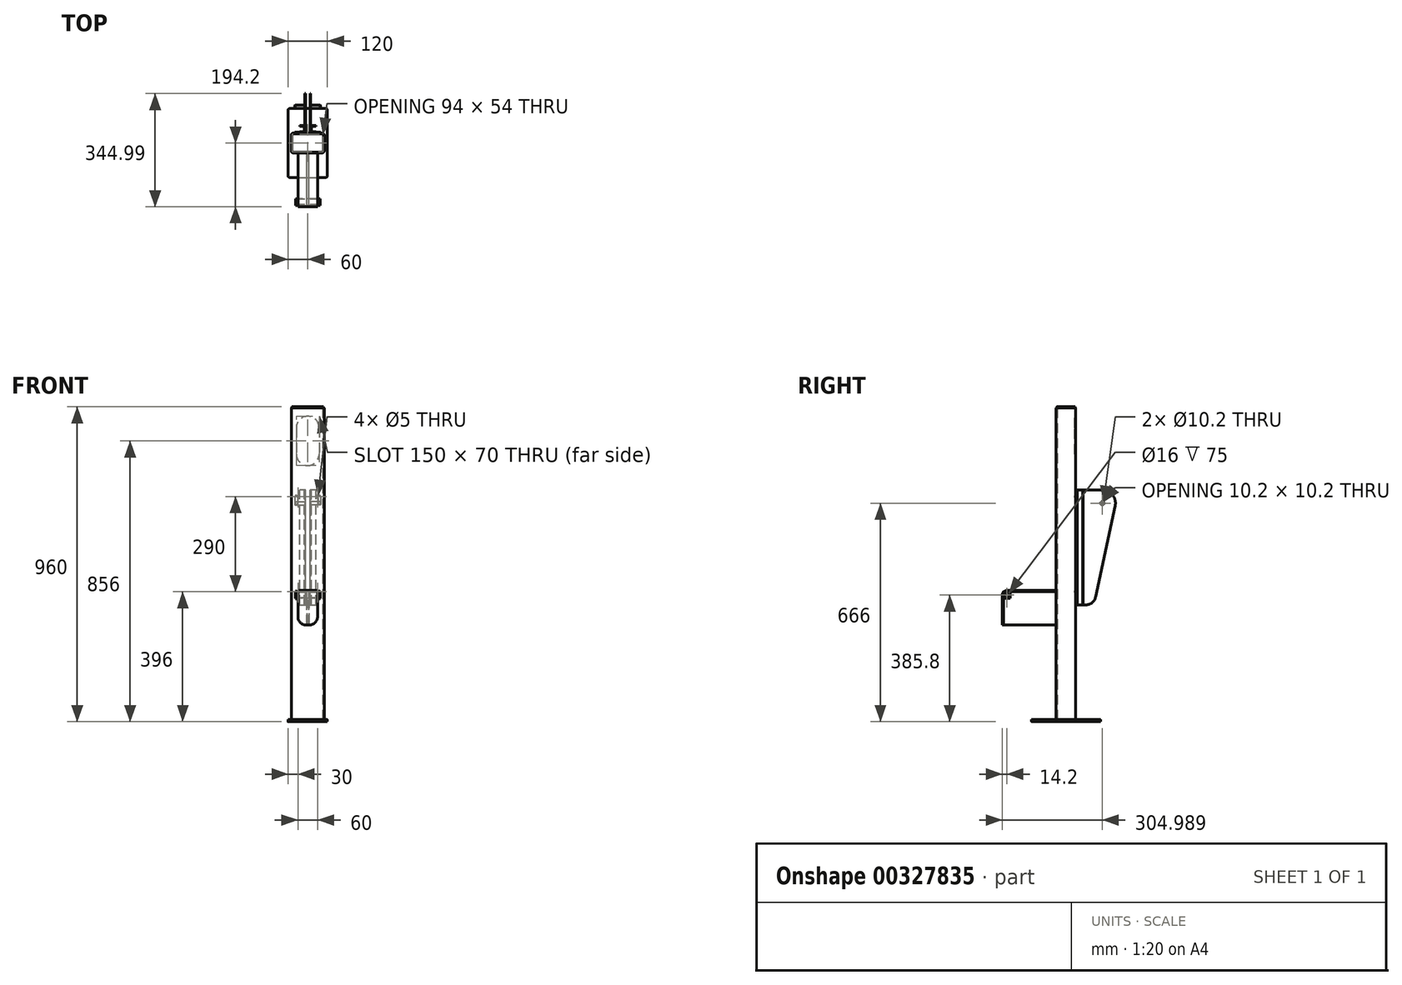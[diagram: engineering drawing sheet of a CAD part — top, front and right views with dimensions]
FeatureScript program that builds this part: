
annotation { "Feature Type Name" : "Feature", "Feature Type Description" : "" }
export const myFeature = defineFeature(function(context is Context, id is Id, definition is map)
    precondition{}
    {
        {
            var Q0;
            Q0=qCreatedBy(makeId("Top.planeOp"),FACE);
            var sketch = newSketch(context, id + "F0", { "sketchPlane" : qUnion([Q0])});
            skLineSegment(sketch, "E0.bottom", {"start": v(50, -30) * mm, "end": v(-50, -30) * mm});
            skLineSegment(sketch, "E0.top", {"start": v(50, 30) * mm, "end": v(-50, 30) * mm});
            skLineSegment(sketch, "E0.left", {"start": v(50, -30) * mm, "end": v(50, 30) * mm});
            skLineSegment(sketch, "E0.right", {"start": v(-50, -30) * mm, "end": v(-50, 30) * mm});
            skPoint(sketch, "E0.middle", {"position": v(0, 0) * mm});
            skSolve(sketch);
        }
        {
            var Q0;
            Q0=makeQuery(id+"F0.imprint","IMPRINT",FACE,{"disambiguationData":[TD([[makeQuery(id+"F0.imprint","IMPRINT",EDGE,{"derivedFrom":sQuery(id+"F0.wireOp",EDGE,"E0.bottom")}),-1.0]])]});
            extrude(context, id + "F1", {"entities" : qUnion([Q0]), "depth" : 950 * mm});
        }
        {
            var Q0;
            Q0=makeQuery(id+"F1.opExtrude","SWEPT_EDGE",EDGE,{"disambiguationData":[OSD([sQuery(id+"F0.wireOp",EDGE,"E0.bottom"),sQuery(id+"F0.wireOp",EDGE,"E0.right")])]});
            var Q1;
            Q1=makeQuery(id+"F1.opExtrude","SWEPT_EDGE",EDGE,{"disambiguationData":[OSD([sQuery(id+"F0.wireOp",EDGE,"E0.top"),sQuery(id+"F0.wireOp",EDGE,"E0.right")])]});
            var Q2;
            Q2=makeQuery(id+"F1.opExtrude","SWEPT_EDGE",EDGE,{"disambiguationData":[OSD([sQuery(id+"F0.wireOp",EDGE,"E0.bottom"),sQuery(id+"F0.wireOp",EDGE,"E0.left")])]});
            var Q3;
            Q3=makeQuery(id+"F1.opExtrude","SWEPT_EDGE",EDGE,{"disambiguationData":[OSD([sQuery(id+"F0.wireOp",EDGE,"E0.top"),sQuery(id+"F0.wireOp",EDGE,"E0.left")])]});
            fillet(context, id + "F2", {"entities" : qUnion([Q0, Q1, Q2, Q3]), "radius" : 5 * mm, "tangentPropagation" : true, "allowEdgeOverflow" : false});
        }
        {
            var Q0;
            Q0=makeQuery(id+"F1.opExtrude","CAP_FACE",FACE,{"disambiguationData":[OSD([sQuery(id+"F0.wireOp",EDGE,"E0.bottom"),sQuery(id+"F0.wireOp",EDGE,"E0.top"),sQuery(id+"F0.wireOp",EDGE,"E0.left"),sQuery(id+"F0.wireOp",EDGE,"E0.right")])],"isStart":true});
            var Q1;
            Q1=makeQuery(id+"F1.opExtrude","CAP_FACE",FACE,{"disambiguationData":[OSD([sQuery(id+"F0.wireOp",EDGE,"E0.bottom"),sQuery(id+"F0.wireOp",EDGE,"E0.top"),sQuery(id+"F0.wireOp",EDGE,"E0.left"),sQuery(id+"F0.wireOp",EDGE,"E0.right")])],"isStart":false});
            shell(context, id + "F3", {"entities" : qUnion([Q0, Q1]), "thickness" : 3 * mm});
        }
        {
            var Q0;
            Q0=makeQuery(id+"F1.opExtrude","SWEPT_FACE",FACE,{"disambiguationData":[OSD([sQuery(id+"F0.wireOp",EDGE,"E0.top")])]});
            var sketch = newSketch(context, id + "F4", { "sketchPlane" : qUnion([Q0])});
            skLineSegment(sketch, "E1", {"start": v(0, 890) * mm, "end": v(0, 810) * mm, "construction": true});
            skArc(sketch, "E2.0.startCap", {"start": v(-35, 890) * mm, "mid": v(0, 925) * mm, "end": v(35, 890) * mm});
            skArc(sketch, "E2.0.endCap", {"start": v(35, 810) * mm, "mid": v(0, 775) * mm, "end": v(-35, 810) * mm});
            skLineSegment(sketch, "E2.0.left", {"start": v(35, 890) * mm, "end": v(35, 810) * mm});
            skLineSegment(sketch, "E2.0.right", {"start": v(-35, 890) * mm, "end": v(-35, 810) * mm});
            skSolve(sketch);
        }
        {
            var Q0;
            Q0 = qSketchRegion(id + "F4", true);
            extrude(context, id + "F5", {"entities" : qUnion([Q0]), "operationType" : NewBodyOperationType.REMOVE, "oppositeDirection" : true, "depth" : 25 * mm});
        }
        {
            var Q0;
            Q0=makeQuery(id+"F1.opExtrude","CAP_FACE",FACE,{"disambiguationData":[OSD([sQuery(id+"F0.wireOp",EDGE,"E0.bottom"),sQuery(id+"F0.wireOp",EDGE,"E0.top"),sQuery(id+"F0.wireOp",EDGE,"E0.left"),sQuery(id+"F0.wireOp",EDGE,"E0.right")])],"isStart":false});
            var sketch = newSketch(context, id + "F6", { "sketchPlane" : qUnion([Q0])});
            skLineSegment(sketch, "E3.bottom", {"start": v(-45, 28) * mm, "end": v(45, 28) * mm});
            skLineSegment(sketch, "E3.top", {"start": v(-45, -28) * mm, "end": v(45, -28) * mm});
            skLineSegment(sketch, "E3.left", {"start": v(-48, 25) * mm, "end": v(-48, -25) * mm});
            skLineSegment(sketch, "E3.right", {"start": v(48, 25) * mm, "end": v(48, -25) * mm});
            skPoint(sketch, "E3.middle", {"position": v(0, 0) * mm});
            skPoint(sketch, "E4.visualSharp", {"position": v(-48, -28) * mm});
            skArc(sketch, "E4.filletArc", {"start": v(-48, -25) * mm, "mid": v(-47.12, -27.12) * mm, "end": v(-45, -28) * mm});
            skPoint(sketch, "E5.visualSharp", {"position": v(48, 28) * mm});
            skArc(sketch, "E5.filletArc", {"start": v(48, 25) * mm, "mid": v(47.12, 27.12) * mm, "end": v(45, 28) * mm});
            skPoint(sketch, "E6.visualSharp", {"position": v(-48, 28) * mm});
            skArc(sketch, "E6.filletArc", {"start": v(-45, 28) * mm, "mid": v(-47.12, 27.12) * mm, "end": v(-48, 25) * mm});
            skPoint(sketch, "E7.visualSharp", {"position": v(48, -28) * mm});
            skArc(sketch, "E7.filletArc", {"start": v(45, -28) * mm, "mid": v(47.12, -27.12) * mm, "end": v(48, -25) * mm});
            skSolve(sketch);
        }
        {
            var Q0;
            Q0=makeQuery(id+"F6.imprint","IMPRINT",FACE,{"disambiguationData":[TD([[makeQuery(id+"F6.imprint","IMPRINT",EDGE,{"derivedFrom":sQuery(id+"F6.wireOp",EDGE,"E3.bottom")}),-1.0]])]});
            var Q1;
            {var subQ3=sQuery(id+"F0.wireOp",EDGE,"E0.bottom");Q1=makeQuery(id+"F6.imprint","IMPRINT",FACE,{"disambiguationData":[TD([[makeQuery(id+"F6.imprint","IMPRINT",EDGE,{"derivedFrom":makeQuery(id+"F3.opShell","OFFSET_EDGE",EDGE,{"disambiguationData":[OSD([subQ3]),TDD([makeQuery(id+"F1.opExtrude","CAP_EDGE",EDGE,{"disambiguationData":[OSD([subQ3])],"isStart":false})])]})}),-1.0]])]});}
            extrude(context, id + "F7", {"entities" : qUnion([Q0, Q1]), "depth" : 4 * mm});
        }
        {
            var Q0;
            Q0=makeQuery(id+"F7.opExtrude","CAP_FACE",FACE,{"disambiguationData":[OSD([sQuery(id+"F6.wireOp",EDGE,"E3.bottom"),sQuery(id+"F6.wireOp",EDGE,"E3.top"),sQuery(id+"F6.wireOp",EDGE,"E3.left"),sQuery(id+"F6.wireOp",EDGE,"E3.right"),sQuery(id+"F6.wireOp",EDGE,"E4.filletArc"),sQuery(id+"F6.wireOp",EDGE,"E5.filletArc"),sQuery(id+"F6.wireOp",EDGE,"E6.filletArc"),sQuery(id+"F6.wireOp",EDGE,"E7.filletArc")])],"isStart":false});
            cPlane(context, id + "F8", {"entities" : qUnion([Q0]), "cplaneType" : CPlaneType.OFFSET, "offset" : 254 * mm, "oppositeDirection" : true, "width" : 150 * mm, "height" : 150 * mm});
        }
        {
            var Q0;
            Q0=qCreatedBy(id+"F8.planeOp",FACE);
            var sketch = newSketch(context, id + "F9", { "sketchPlane" : qUnion([Q0])});
            skLineSegment(sketch, "E8", {"start": v(-45, 32.79) * mm, "end": v(-10.5, 32.79) * mm});
            skLineSegment(sketch, "E9", {"start": v(-9, 34.3) * mm, "end": v(-9, 190.79) * mm});
            skLineSegment(sketch, "E10.0", {"start": v(-7, 34.3) * mm, "end": v(-7, 190.79) * mm});
            skLineSegment(sketch, "E10.1", {"start": v(-45, 30.79) * mm, "end": v(-10.5, 30.79) * mm});
            skPoint(sketch, "E11.visualSharp", {"position": v(-9, 32.79) * mm});
            skArc(sketch, "E11.filletArc", {"start": v(-10.5, 32.79) * mm, "mid": v(-9.44, 33.23) * mm, "end": v(-9, 34.3) * mm});
            skLineSegment(sketch, "E12", {"start": v(-7, 190.79) * mm, "end": v(-9, 190.79) * mm});
            skLineSegment(sketch, "E13", {"start": v(-45, 30.79) * mm, "end": v(-45, 32.79) * mm});
            skArc(sketch, "E14.0", {"start": v(-10.5, 30.79) * mm, "mid": v(-8.03, 31.82) * mm, "end": v(-7, 34.3) * mm});
            skSolve(sketch);
        }
        {
            var Q0;
            Q0=makeQuery(id+"F9.imprint","IMPRINT",FACE,{"disambiguationData":[TD([[makeQuery(id+"F9.imprint","IMPRINT",EDGE,{"derivedFrom":sQuery(id+"F9.wireOp",EDGE,"E8")}),-1.0]])]});
            extrude(context, id + "F10", {"entities" : qUnion([Q0]), "oppositeDirection" : true, "depth" : 350 * mm});
        }
        {
            var Q0;
            Q0=makeQuery(id+"F10.opExtrude","SWEPT_FACE",FACE,{"disambiguationData":[OSD([sQuery(id+"F9.wireOp",EDGE,"E9")])]});
            var sketch = newSketch(context, id + "F11", { "sketchPlane" : qUnion([Q0])});
            skSolve(sketch);
        }
        {
            var Q0;
            {var subQ0=sQuery(id+"F9.wireOp",EDGE,"E9");Q0=makeQuery(id+"F11.imprint","IMPRINT",FACE,{"disambiguationData":[TD([[makeQuery(id+"F11.imprint","IMPRINT",EDGE,{"derivedFrom":makeQuery(id+"F10.opExtrude","CAP_EDGE",EDGE,{"disambiguationData":[OSD([subQ0])],"isStart":true})}),1.0]])]});}
            var sketch = newSketch(context, id + "F12", { "sketchPlane" : qUnion([Q0])});
            skLineSegment(sketch, "E15", {"start": v(-30.79, 700) * mm, "end": v(-110.79, 700) * mm});
            skArc(sketch, "E16", {"start": v(-110.79, 700) * mm, "mid": v(-141.9, 685.13) * mm, "end": v(-149.9, 651.59) * mm});
            skLineSegment(sketch, "E17", {"start": v(-149.9, 651.59) * mm, "end": v(-90.12, 373.7) * mm});
            skLineSegment(sketch, "E18", {"start": v(-60.79, 350) * mm, "end": v(-30.79, 350) * mm});
            skPoint(sketch, "E19.visualSharp", {"position": v(-85.02, 350) * mm});
            skArc(sketch, "E19.filletArc", {"start": v(-90.12, 373.7) * mm, "mid": v(-79.64, 356.66) * mm, "end": v(-60.79, 350) * mm});
            skLineSegment(sketch, "E20", {"start": v(-30.79, 700) * mm, "end": v(-30.79, 788.18) * mm});
            skLineSegment(sketch, "E21", {"start": v(-30.79, 788.18) * mm, "end": v(-387.89, 788.18) * mm});
            skLineSegment(sketch, "E22", {"start": v(-387.89, 788.18) * mm, "end": v(-387.89, 182.91) * mm});
            skLineSegment(sketch, "E23", {"start": v(-387.89, 182.91) * mm, "end": v(-30.79, 182.91) * mm});
            skLineSegment(sketch, "E24", {"start": v(-30.79, 182.91) * mm, "end": v(-30.79, 350) * mm});
            skPoint(sketch, "E25.orphan", {"position": v(0, 182.91) * mm});
            skCircle(sketch, "E26", {"center": v(-110.79, 660) * mm, "radius": 5.1 * mm});
            skSolve(sketch);
        }
        {
            var Q0;
            Q0 = qSketchRegion(id + "F12", true);
            extrude(context, id + "F13", {"entities" : qUnion([Q0]), "operationType" : NewBodyOperationType.REMOVE, "oppositeDirection" : true, "depth" : 25 * mm});
        }
        {
            var Q0;
            Q0=makeQuery(id+"F10.opExtrude","CAP_EDGE",EDGE,{"disambiguationData":[OSD([sQuery(id+"F9.wireOp",EDGE,"E13")])],"isStart":true});
            var Q1;
            Q1=makeQuery(id+"F10.opExtrude","CAP_EDGE",EDGE,{"disambiguationData":[OSD([sQuery(id+"F9.wireOp",EDGE,"E13")])],"isStart":false});
            fillet(context, id + "F14", {"entities" : qUnion([Q0, Q1]), "radius" : 10 * mm, "allowEdgeOverflow" : false});
        }
        {
            var Q0;
            Q0=makeQuery(id+"F10.opExtrude","SWEPT_FACE",FACE,{"disambiguationData":[OSD([sQuery(id+"F9.wireOp",EDGE,"E8")])]});
            var sketch = newSketch(context, id + "F15", { "sketchPlane" : qUnion([Q0])});
            skLineSegment(sketch, "E27", {"start": v(35, 680) * mm, "end": v(35, 370) * mm, "construction": true});
            skPoint(sketch, "E27.startSnap0", {"position": v(35, 700) * mm});
            skLineSegment(sketch, "E28", {"start": v(35, 370) * mm, "end": v(35, 390) * mm, "construction": true});
            skArc(sketch, "E29.0.startCap", {"start": v(39, 370) * mm, "mid": v(35, 366) * mm, "end": v(31, 370) * mm});
            skArc(sketch, "E29.0.endCap", {"start": v(35, 394) * mm, "mid": v(37.83, 392.83) * mm, "end": v(39, 390) * mm});
            skLineSegment(sketch, "E29.0.left", {"start": v(31, 370) * mm, "end": v(31, 386) * mm});
            skLineSegment(sketch, "E29.0.right", {"start": v(39, 370) * mm, "end": v(39, 390) * mm});
            skLineSegment(sketch, "E30", {"start": v(35, 680) * mm, "end": v(35, 660) * mm, "construction": true});
            skArc(sketch, "E31.0.startCap", {"start": v(35, 684) * mm, "mid": v(37.83, 682.83) * mm, "end": v(39, 680) * mm});
            skArc(sketch, "E31.0.endCap", {"start": v(39, 660) * mm, "mid": v(35, 656) * mm, "end": v(31, 660) * mm});
            skLineSegment(sketch, "E31.0.left", {"start": v(39, 680) * mm, "end": v(39, 660) * mm});
            skLineSegment(sketch, "E31.0.right", {"start": v(31, 676) * mm, "end": v(31, 660) * mm});
            skLineSegment(sketch, "E32", {"start": v(35, 680) * mm, "end": v(30, 680) * mm, "construction": true});
            skArc(sketch, "E33.0.endCap", {"start": v(30, 676) * mm, "mid": v(26, 680) * mm, "end": v(30, 684) * mm});
            skLineSegment(sketch, "E33.0.left", {"start": v(31, 676) * mm, "end": v(30, 676) * mm});
            skLineSegment(sketch, "E33.0.right", {"start": v(35, 684) * mm, "end": v(30, 684) * mm});
            skLineSegment(sketch, "E34", {"start": v(35, 390) * mm, "end": v(30, 390) * mm, "construction": true});
            skArc(sketch, "E35.0.endCap", {"start": v(30, 386) * mm, "mid": v(26, 390) * mm, "end": v(30, 394) * mm});
            skLineSegment(sketch, "E35.0.left", {"start": v(31, 386) * mm, "end": v(30, 386) * mm});
            skLineSegment(sketch, "E35.0.right", {"start": v(35, 394) * mm, "end": v(30, 394) * mm});
            skSolve(sketch);
        }
        {
            var Q0;
            Q0=makeQuery(id+"F15.imprint","IMPRINT",FACE,{"disambiguationData":[TD([[makeQuery(id+"F15.imprint","IMPRINT",EDGE,{"derivedFrom":sQuery(id+"F15.wireOp",EDGE,"E31.0.endCap")}),-1.0]])]});
            var Q1;
            Q1=makeQuery(id+"F15.imprint","IMPRINT",FACE,{"disambiguationData":[TD([[makeQuery(id+"F15.imprint","IMPRINT",EDGE,{"derivedFrom":sQuery(id+"F15.wireOp",EDGE,"E29.0.startCap")}),-1.0]])]});
            extrude(context, id + "F16", {"entities" : qUnion([Q0, Q1]), "operationType" : NewBodyOperationType.REMOVE, "endBound" : BoundingType.UP_TO_NEXT, "oppositeDirection" : true, "depth" : 25 * mm});
        }
        {
            var Q0;
            Q0=makeQuery(id+"F1.opExtrude","CAP_FACE",FACE,{"disambiguationData":[OSD([sQuery(id+"F0.wireOp",EDGE,"E0.bottom"),sQuery(id+"F0.wireOp",EDGE,"E0.top"),sQuery(id+"F0.wireOp",EDGE,"E0.left"),sQuery(id+"F0.wireOp",EDGE,"E0.right")])],"isStart":true});
            var sketch = newSketch(context, id + "F17", { "sketchPlane" : qUnion([Q0])});
            skLineSegment(sketch, "E36.bottom", {"start": v(-55, 105) * mm, "end": v(55, 105) * mm});
            skLineSegment(sketch, "E36.top", {"start": v(-55, -105) * mm, "end": v(55, -105) * mm});
            skLineSegment(sketch, "E36.left", {"start": v(-60, 100) * mm, "end": v(-60, -100) * mm});
            skLineSegment(sketch, "E36.right", {"start": v(60, 100) * mm, "end": v(60, -100) * mm});
            skPoint(sketch, "E36.middle", {"position": v(0, 0) * mm});
            skPoint(sketch, "E37.visualSharp", {"position": v(60, -105) * mm});
            skArc(sketch, "E37.filletArc", {"start": v(55, -105) * mm, "mid": v(58.54, -103.54) * mm, "end": v(60, -100) * mm});
            skPoint(sketch, "E38.visualSharp", {"position": v(-60, -105) * mm});
            skArc(sketch, "E38.filletArc", {"start": v(-60, -100) * mm, "mid": v(-58.54, -103.54) * mm, "end": v(-55, -105) * mm});
            skPoint(sketch, "E39.visualSharp", {"position": v(60, 105) * mm});
            skArc(sketch, "E39.filletArc", {"start": v(60, 100) * mm, "mid": v(58.54, 103.54) * mm, "end": v(55, 105) * mm});
            skPoint(sketch, "E40.visualSharp", {"position": v(-60, 105) * mm});
            skArc(sketch, "E40.filletArc", {"start": v(-55, 105) * mm, "mid": v(-58.54, 103.54) * mm, "end": v(-60, 100) * mm});
            skSolve(sketch);
        }
        {
            var Q0;
            Q0 = qSketchRegion(id + "F17", true);
            extrude(context, id + "F18", {"entities" : qUnion([Q0]), "depth" : 6 * mm});
        }
        {
            var Q0;
            {var subQ4=sQuery(id+"F12.wireOp",EDGE,"E16");Q0=makeQuery(id+"F12.imprint","IMPRINT",FACE,{"disambiguationData":[TD([[makeQuery(id+"F12.imprint","IMPRINT",EDGE,{"derivedFrom":subQ4}),1.0]])]});}
            var sketch = newSketch(context, id + "F19", { "sketchPlane" : qUnion([Q0])});
            skCircle(sketch, "E41", {"center": v(-110.79, 660) * mm, "radius": 5 * mm});
            skSolve(sketch);
        }
        {
            var Q0;
            Q0 = qSketchRegion(id + "F19", true);
            extrude(context, id + "F20", {"entities" : qUnion([Q0]), "operationType" : NewBodyOperationType.ADD, "depth" : 30 * mm});
        }
        {
            var Q0;
            Q0=qCreatedBy(id+"F8.planeOp",FACE);
            var sketch = newSketch(context, id + "F21", { "sketchPlane" : qUnion([Q0])});
            skLineSegment(sketch, "E42", {"start": v(-25, 32.79) * mm, "end": v(-12.5, 32.79) * mm});
            skLineSegment(sketch, "E43", {"start": v(-9, 36.3) * mm, "end": v(-9, 49.28) * mm});
            skLineSegment(sketch, "E44", {"start": v(-12.51, 52.79) * mm, "end": v(-25, 52.79) * mm});
            skLineSegment(sketch, "E45", {"start": v(-25, 52.79) * mm, "end": v(-25, 50.79) * mm});
            skLineSegment(sketch, "E46", {"start": v(-25, 50.79) * mm, "end": v(-12.5, 50.79) * mm});
            skLineSegment(sketch, "E47", {"start": v(-11, 49.28) * mm, "end": v(-11, 36.3) * mm});
            skLineSegment(sketch, "E48", {"start": v(-12.5, 34.79) * mm, "end": v(-25, 34.79) * mm});
            skLineSegment(sketch, "E49", {"start": v(-25, 34.79) * mm, "end": v(-25, 32.79) * mm});
            skPoint(sketch, "E50.visualSharp", {"position": v(-11, 34.79) * mm});
            skArc(sketch, "E50.filletArc", {"start": v(-12.5, 34.79) * mm, "mid": v(-11.44, 35.23) * mm, "end": v(-11, 36.3) * mm});
            skPoint(sketch, "E51.visualSharp", {"position": v(-11, 50.79) * mm});
            skArc(sketch, "E51.filletArc", {"start": v(-11, 49.28) * mm, "mid": v(-11.44, 50.35) * mm, "end": v(-12.5, 50.79) * mm});
            skPoint(sketch, "E52.visualSharp", {"position": v(-9, 52.79) * mm});
            skArc(sketch, "E52.filletArc", {"start": v(-9, 49.28) * mm, "mid": v(-10.03, 51.76) * mm, "end": v(-12.51, 52.79) * mm});
            skPoint(sketch, "E53.visualSharp", {"position": v(-9, 32.79) * mm});
            skArc(sketch, "E53.filletArc", {"start": v(-12.5, 32.79) * mm, "mid": v(-10.03, 33.82) * mm, "end": v(-9, 36.3) * mm});
            skSolve(sketch);
        }
        {
            var Q0;
            Q0=makeQuery(id+"F20.opExtrude","CAP_FACE",FACE,{"disambiguationData":[OSD([sQuery(id+"F19.wireOp",EDGE,"E41")])],"isStart":false});
            chamfer(context, id + "F22", {"entities" : qUnion([Q0]), "width" : 1 * mm, "tangentPropagation" : true});
        }
        {
            var Q0;
            Q0 = qSketchRegion(id + "F21", true);
            extrude(context, id + "F23", {"entities" : qUnion([Q0]), "operationType" : NewBodyOperationType.ADD, "oppositeDirection" : true, "depth" : 350 * mm});
        }
        {
            var Q0;
            Q0=makeQuery(id+"F10.opExtrude","SWEPT_BODY",BODY,{"disambiguationData":[OSD([sQuery(id+"F9.wireOp",EDGE,"E8"),sQuery(id+"F9.wireOp",EDGE,"E9"),sQuery(id+"F9.wireOp",EDGE,"E10.0"),sQuery(id+"F9.wireOp",EDGE,"E10.1"),sQuery(id+"F9.wireOp",EDGE,"E11.filletArc"),sQuery(id+"F9.wireOp",EDGE,"E12"),sQuery(id+"F9.wireOp",EDGE,"E13"),sQuery(id+"F9.wireOp",EDGE,"E14.0")])]});
            var Q1;
            Q1=makeQuery(id+"F20.opExtrude","SWEPT_BODY",BODY,{"disambiguationData":[OSD([sQuery(id+"F19.wireOp",EDGE,"E41")])]});
            var Q2;
            Q2=qCreatedBy(makeId("Right.planeOp"),FACE);
            mirror(context, id + "F24", {"entities" : qUnion([Q0, Q1]), "mirrorPlane" : qUnion([Q2])});
        }
        {
            var Q0;
            Q0=makeQuery(id+"F4.imprint","IMPRINT",FACE,{"disambiguationData":[TD([[makeQuery(id+"F4.imprint","IMPRINT",EDGE,{"derivedFrom":sQuery(id+"F4.wireOp",EDGE,"E2.0.startCap")}),1.0]])]});
            var sketch = newSketch(context, id + "F25", { "sketchPlane" : qUnion([Q0])});
            skCircle(sketch, "E54", {"center": v(-30, 680) * mm, "radius": 2.5 * mm});
            skCircle(sketch, "E55", {"center": v(30, 680) * mm, "radius": 2.5 * mm});
            skCircle(sketch, "E56", {"center": v(-30, 390) * mm, "radius": 2.5 * mm});
            skCircle(sketch, "E57", {"center": v(30, 390) * mm, "radius": 2.5 * mm});
            skSolve(sketch);
        }
        {
            var Q0;
            Q0 = qSketchRegion(id + "F25", true);
            extrude(context, id + "F26", {"entities" : qUnion([Q0]), "operationType" : NewBodyOperationType.REMOVE, "endBound" : BoundingType.UP_TO_NEXT, "oppositeDirection" : true, "depth" : 25 * mm});
        }
        {
            var Q0;
            Q0=qCreatedBy(makeId("Right.planeOp"),FACE);
            var sketch = newSketch(context, id + "F27", { "sketchPlane" : qUnion([Q0])});
            skLineSegment(sketch, "E58", {"start": v(-190.2, 288.84) * mm, "end": v(-190.2, 379.8) * mm});
            skLineSegment(sketch, "E59", {"start": v(-180, 390) * mm, "end": v(-30, 390) * mm});
            skLineSegment(sketch, "E60", {"start": v(-30, 390) * mm, "end": v(-190.2, 288.84) * mm, "construction": true});
            skPoint(sketch, "E61.visualSharp", {"position": v(-190.2, 390) * mm});
            skArc(sketch, "E61.filletArc", {"start": v(-180, 390) * mm, "mid": v(-187.21, 387.01) * mm, "end": v(-190.2, 379.8) * mm});
            skLineSegment(sketch, "E62.0", {"start": v(-180, 394) * mm, "end": v(-30, 394) * mm});
            skArc(sketch, "E62.1", {"start": v(-180, 394) * mm, "mid": v(-190.04, 389.84) * mm, "end": v(-194.2, 379.8) * mm});
            skLineSegment(sketch, "E62.2", {"start": v(-194.2, 288.84) * mm, "end": v(-194.2, 379.8) * mm});
            skLineSegment(sketch, "E63", {"start": v(-30, 390) * mm, "end": v(-30, 394) * mm});
            skLineSegment(sketch, "E64", {"start": v(-194.2, 288.84) * mm, "end": v(-190.2, 288.84) * mm});
            skSolve(sketch);
        }
        {
            var Q0;
            Q0=makeQuery(id+"F27.imprint","IMPRINT",FACE,{"disambiguationData":[TD([[makeQuery(id+"F27.imprint","IMPRINT",EDGE,{"derivedFrom":sQuery(id+"F27.wireOp",EDGE,"E58")}),1.0]])]});
            extrude(context, id + "F28", {"entities" : qUnion([Q0]), "endBound" : BoundingType.SYMMETRIC, "depth" : 60 * mm});
        }
        {
            var Q0;
            Q0=qCreatedBy(makeId("Right.planeOp"),FACE);
            var sketch = newSketch(context, id + "F29", { "sketchPlane" : qUnion([Q0])});
            skLineSegment(sketch, "E65.2", {"start": v(-170.2, 390) * mm, "end": v(-30, 390) * mm});
            skPoint(sketch, "E65.1.center.orphan", {"position": v(-180, 261.33) * mm});
            skLineSegment(sketch, "E66", {"start": v(-190.2, 370) * mm, "end": v(-190.2, 288.84) * mm});
            skLineSegment(sketch, "E67", {"start": v(-190.2, 288.84) * mm, "end": v(-190.2, 288.84) * mm});
            skLineSegment(sketch, "E68", {"start": v(-190.2, 370) * mm, "end": v(-170.2, 370) * mm});
            skPoint(sketch, "E68.endSnap0", {"position": v(-170.2, 362.18) * mm});
            skLineSegment(sketch, "E69", {"start": v(-170.2, 370) * mm, "end": v(-170.2, 390) * mm});
            skPoint(sketch, "E70.orphan", {"position": v(-190.2, 379.8) * mm});
            skPoint(sketch, "E71.orphan", {"position": v(-180, 390) * mm});
            skPoint(sketch, "E72.center.orphan", {"position": v(-180, 379.8) * mm});
            skLineSegment(sketch, "E73", {"start": v(-190.2, 288.84) * mm, "end": v(-30, 288.84) * mm});
            skLineSegment(sketch, "E74", {"start": v(-30, 288.84) * mm, "end": v(-30, 390) * mm});
            skSolve(sketch);
        }
        {
            var Q0;
            Q0 = qSketchRegion(id + "F29", true);
            extrude(context, id + "F30", {"entities" : qUnion([Q0]), "endBound" : BoundingType.SYMMETRIC, "depth" : 6 * mm});
        }
        {
            var Q0;
            Q0=qCreatedBy(makeId("Right.planeOp"),FACE);
            var sketch = newSketch(context, id + "F31", { "sketchPlane" : qUnion([Q0])});
            skCircle(sketch, "E75", {"center": v(-180, 379.8) * mm, "radius": 10 * mm});
            skCircle(sketch, "E76.0", {"center": v(-180, 379.8) * mm, "radius": 8 * mm});
            skSolve(sketch);
        }
        {
            var Q0;
            Q0 = qSketchRegion(id + "F31", true);
            extrude(context, id + "F32", {"entities" : qUnion([Q0]), "endBound" : BoundingType.SYMMETRIC, "depth" : 75 * mm});
        }
        {
            var Q0;
            Q0=makeQuery(id+"F28.opExtrude","CAP_EDGE",EDGE,{"disambiguationData":[OSD([sQuery(id+"F27.wireOp",EDGE,"E64")])],"isStart":false});
            var Q1;
            Q1=makeQuery(id+"F28.opExtrude","CAP_EDGE",EDGE,{"disambiguationData":[OSD([sQuery(id+"F27.wireOp",EDGE,"E64")])],"isStart":true});
            fillet(context, id + "F33", {"entities" : qUnion([Q0, Q1]), "radius" : 25 * mm, "tangentPropagation" : true, "allowEdgeOverflow" : false});
        }
    });
